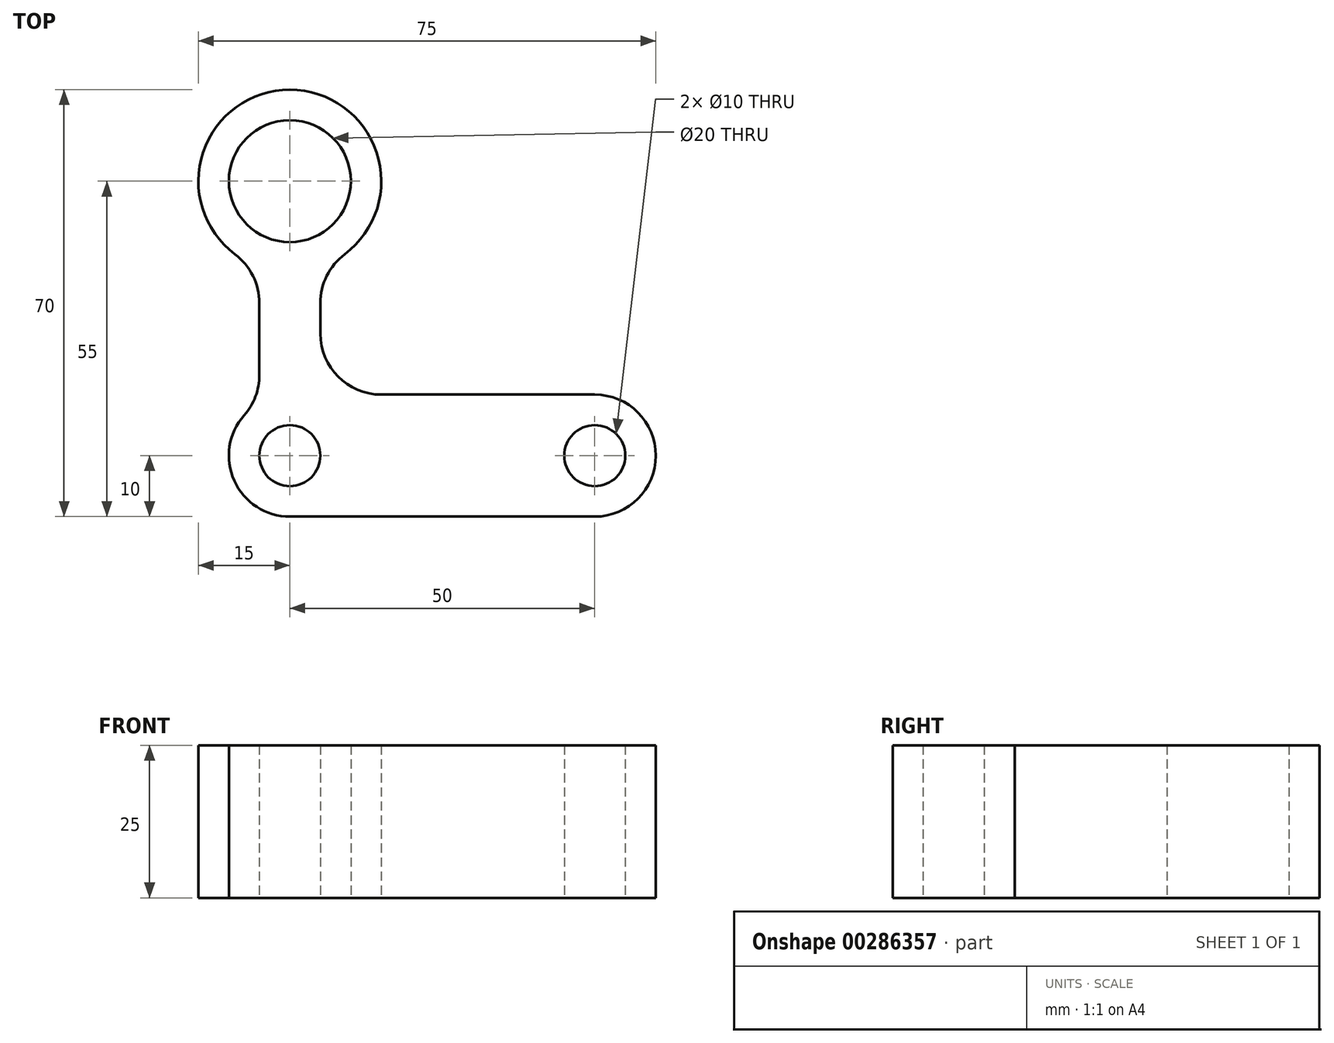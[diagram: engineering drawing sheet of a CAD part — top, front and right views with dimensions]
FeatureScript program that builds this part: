
annotation { "Feature Type Name" : "Feature", "Feature Type Description" : "" }
export const myFeature = defineFeature(function(context is Context, id is Id, definition is map)
    precondition{}
    {
        {
            var Q0;
            Q0=qCreatedBy(makeId("Top.planeOp"),FACE);
            var sketch = newSketch(context, id + "F0", { "sketchPlane" : qUnion([Q0])});
            skLineSegment(sketch, "E0", {"start": v(0, 0) * mm, "end": v(5, 0) * mm});
            skLineSegment(sketch, "E1", {"start": v(0, 0) * mm, "end": v(0, 45) * mm});
            skCircle(sketch, "E2", {"center": v(0, 45) * mm, "radius": 10 * mm});
            skArc(sketch, "E3", {"start": v(9, 33) * mm, "mid": v(0, 60) * mm, "end": v(-9, 33) * mm});
            skCircle(sketch, "E4", {"center": v(0, 0) * mm, "radius": 5 * mm});
            skArc(sketch, "E5", {"start": v(-7.5, 6.61) * mm, "mid": v(-9.11, -4.11) * mm, "end": v(0, -10) * mm});
            skCircle(sketch, "E6", {"center": v(50, 0) * mm, "radius": 5 * mm});
            skArc(sketch, "E7", {"start": v(50, -10) * mm, "mid": v(60, 0) * mm, "end": v(50, 10) * mm});
            skPoint(sketch, "E8.endSnap0", {"position": v(0, 22.5) * mm});
            skPoint(sketch, "E9.visualSharp", {"position": v(-5, 8.66) * mm});
            skArc(sketch, "E9.filletArc", {"start": v(-7.5, 6.61) * mm, "mid": v(-5.65, 9.7) * mm, "end": v(-5, 13.23) * mm});
            skLineSegment(sketch, "E10", {"start": v(50, 10) * mm, "end": v(15, 10) * mm});
            skPoint(sketch, "E11.visualSharp", {"position": v(5, 10) * mm});
            skArc(sketch, "E11.filletArc", {"start": v(5, 20) * mm, "mid": v(7.93, 12.93) * mm, "end": v(15, 10) * mm});
            skLineSegment(sketch, "E12", {"start": v(0, -10) * mm, "end": v(50, -10) * mm});
            skLineSegment(sketch, "E13.trimOffspring", {"start": v(40, 0) * mm, "end": v(50, 0) * mm});
            skPoint(sketch, "E14.visualSharp", {"position": v(5, 30.86) * mm});
            skArc(sketch, "E14.filletArc", {"start": v(9, 33) * mm, "mid": v(6.06, 29.47) * mm, "end": v(5, 25) * mm});
            skPoint(sketch, "E15.visualSharp", {"position": v(-5, 30.86) * mm});
            skArc(sketch, "E15.filletArc", {"start": v(-5, 25) * mm, "mid": v(-6.06, 29.47) * mm, "end": v(-9, 33) * mm});
            skLineSegment(sketch, "E16", {"start": v(-5, 13.23) * mm, "end": v(-5, 25) * mm});
            skLineSegment(sketch, "E17", {"start": v(5, 20) * mm, "end": v(5, 25) * mm});
            skSolve(sketch);
        }
        {
            var Q0;
            Q0=makeQuery(id+"F0.imprint","IMPRINT",FACE,{"disambiguationData":[TD([[makeQuery(id+"F0.imprint","IMPRINT",EDGE,{"derivedFrom":sQuery(id+"F0.wireOp",EDGE,"E2")}),-1.0]])]});
            extrude(context, id + "F1", {"entities" : qUnion([Q0]), "depth" : 25 * mm});
        }
    });
